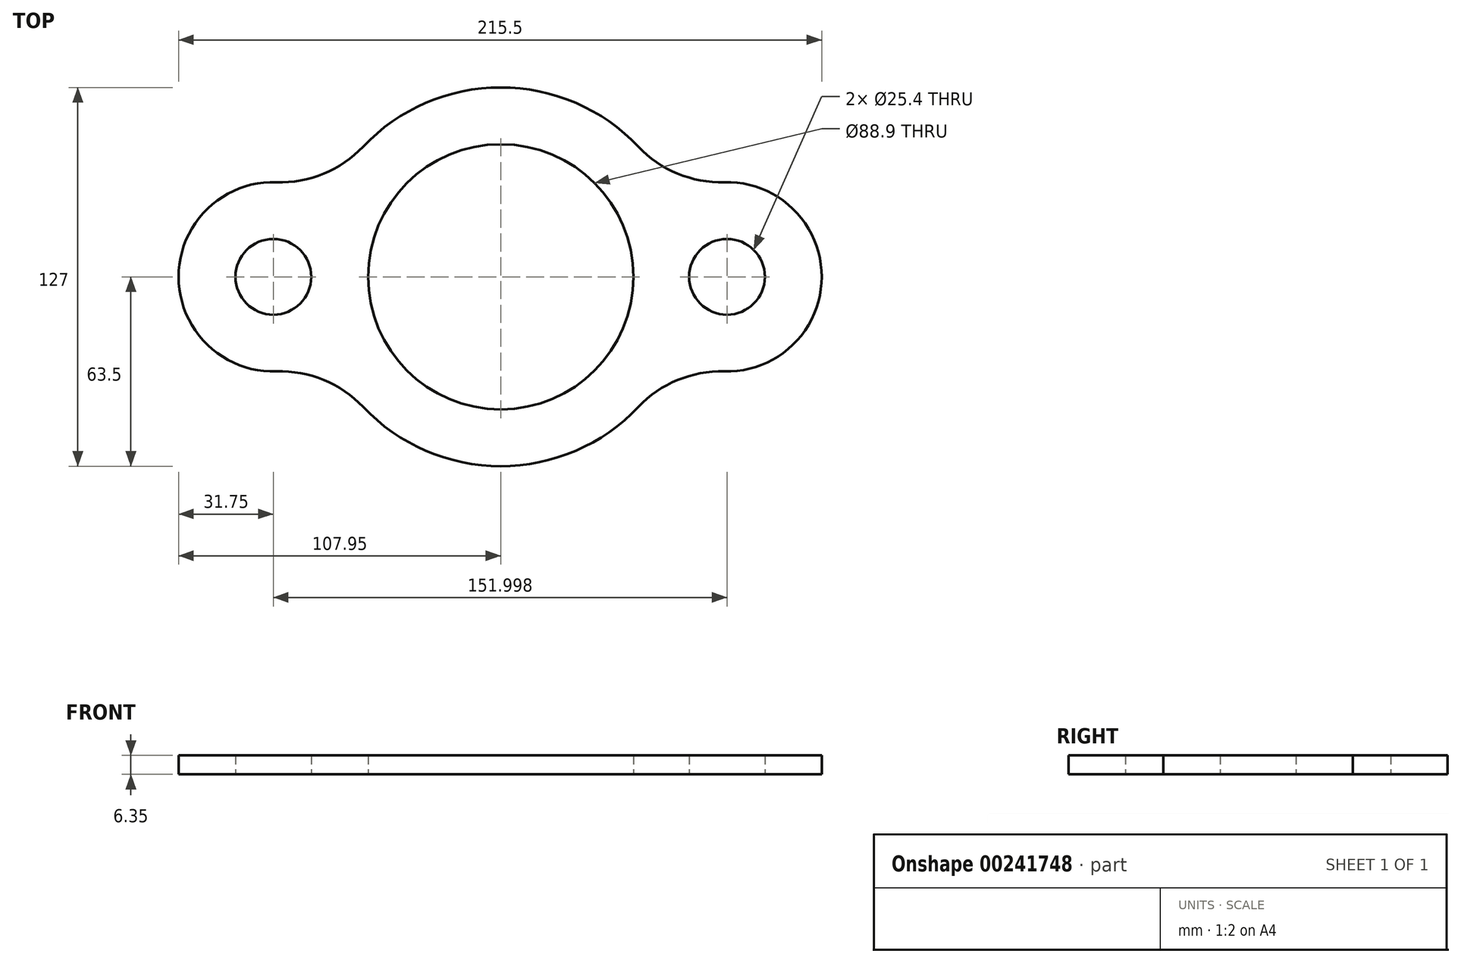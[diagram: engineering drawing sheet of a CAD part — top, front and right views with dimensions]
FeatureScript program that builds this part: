
annotation { "Feature Type Name" : "Feature", "Feature Type Description" : "" }
export const myFeature = defineFeature(function(context is Context, id is Id, definition is map)
    precondition{}
    {
        {
            var Q0;
            Q0=qCreatedBy(makeId("Top.planeOp"),FACE);
            var sketch = newSketch(context, id + "F0", { "sketchPlane" : qUnion([Q0])});
            skCircle(sketch, "E0", {"center": v(0, 0) * mm, "radius": 44.45 * mm});
            skArc(sketch, "E1", {"start": v(-46.14, -43.63) * mm, "mid": v(0, -63.5) * mm, "end": v(46.13, -43.64) * mm});
            skCircle(sketch, "E2", {"center": v(-76.2, 0) * mm, "radius": 12.7 * mm});
            skArc(sketch, "E3", {"start": v(-75.12, 31.73) * mm, "mid": v(-107.95, 0) * mm, "end": v(-75.12, -31.73) * mm});
            skPoint(sketch, "E4.visualSharp", {"position": v(-57.94, 25.98) * mm});
            skArc(sketch, "E4.filletArc", {"start": v(-75.12, 31.73) * mm, "mid": v(-59.35, 34.56) * mm, "end": v(-46.14, 43.63) * mm});
            skPoint(sketch, "E5.visualSharp", {"position": v(-57.94, -25.98) * mm});
            skArc(sketch, "E5.filletArc", {"start": v(-46.14, -43.63) * mm, "mid": v(-59.35, -34.56) * mm, "end": v(-75.12, -31.73) * mm});
            skPoint(sketch, "E6.centerSnap0", {"position": v(63.5, 0) * mm});
            skCircle(sketch, "E7", {"center": v(75.8, 0) * mm, "radius": 12.7 * mm});
            skArc(sketch, "E8.trimOffspring", {"start": v(74.9, -31.74) * mm, "mid": v(107.55, 0) * mm, "end": v(74.9, 31.74) * mm});
            skArc(sketch, "E9.trimOffspring", {"start": v(46.13, 43.64) * mm, "mid": v(0, 63.5) * mm, "end": v(-46.14, 43.63) * mm});
            skArc(sketch, "E10.trimOffspring", {"start": v(63.43, -2.9) * mm, "mid": v(63.5, 0) * mm, "end": v(63.43, 2.9) * mm});
            skPoint(sketch, "E11.visualSharp", {"position": v(57.85, 26.19) * mm});
            skArc(sketch, "E11.filletArc", {"start": v(46.13, 43.64) * mm, "mid": v(59.24, 34.62) * mm, "end": v(74.9, 31.74) * mm});
            skPoint(sketch, "E12.visualSharp", {"position": v(57.85, -26.19) * mm});
            skArc(sketch, "E12.filletArc", {"start": v(74.9, -31.74) * mm, "mid": v(59.24, -34.62) * mm, "end": v(46.13, -43.64) * mm});
            skPoint(sketch, "E13", {"position": v(-78.6, -69.8) * mm});
            skPoint(sketch, "E14", {"position": v(73.78, -72.79) * mm});
            skPoint(sketch, "E15", {"position": v(0, -72.79) * mm});
            skSolve(sketch);
        }
        {
            var Q0;
            Q0=makeQuery(id+"F0.imprint","IMPRINT",FACE,{"disambiguationData":[TD([[makeQuery(id+"F0.imprint","IMPRINT",EDGE,{"derivedFrom":sQuery(id+"F0.wireOp",EDGE,"E0")}),-1.0]])]});
            extrude(context, id + "F1", {"entities" : qUnion([Q0]), "depth" : 6.35 * mm});
        }
    });
